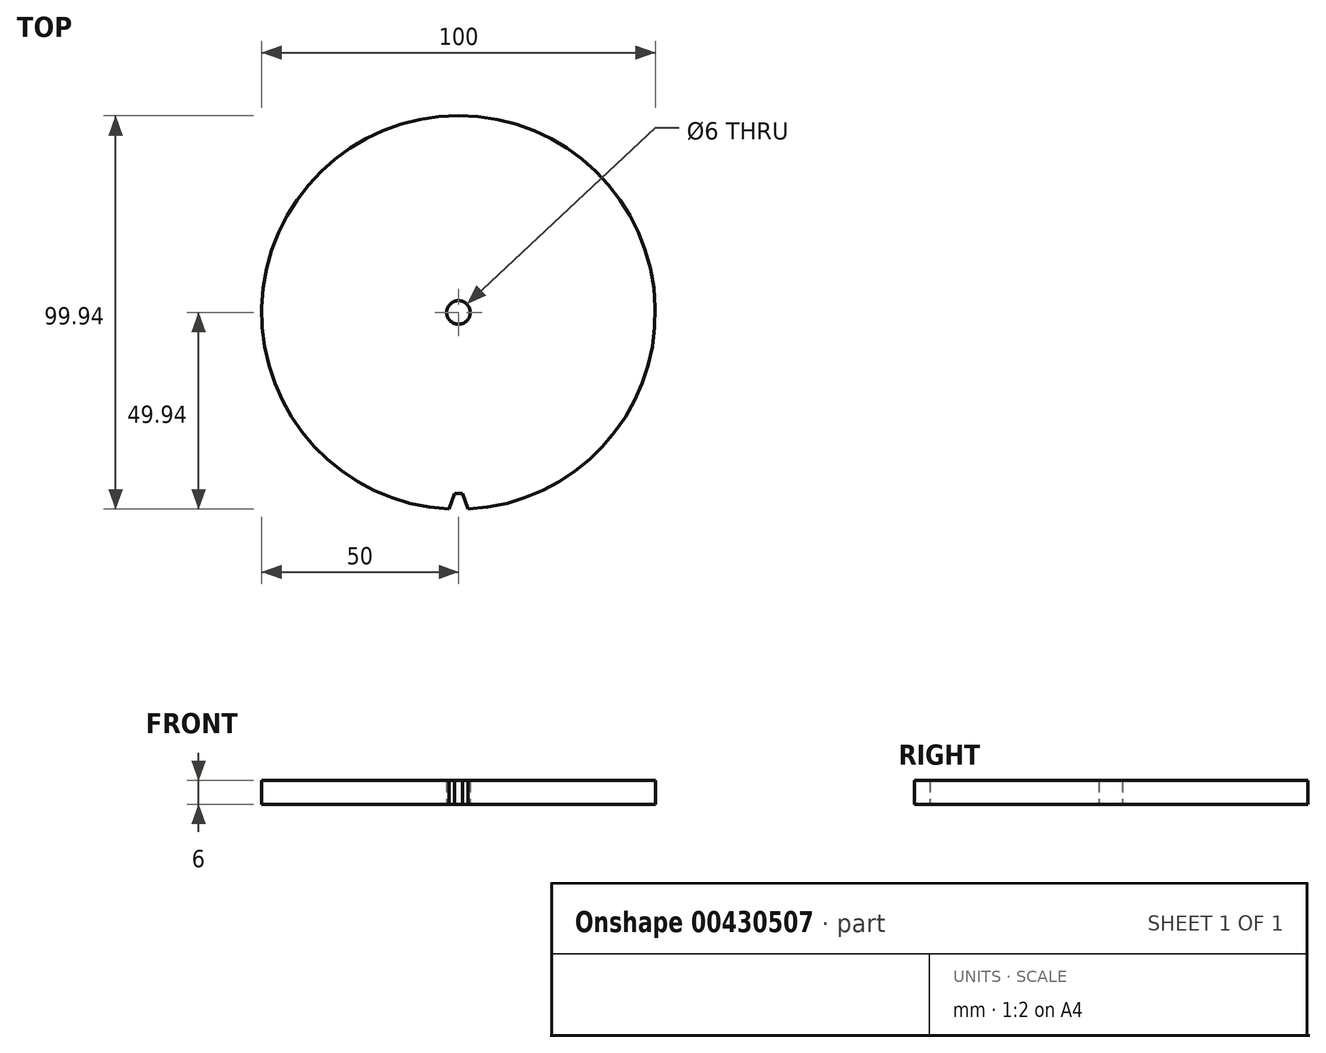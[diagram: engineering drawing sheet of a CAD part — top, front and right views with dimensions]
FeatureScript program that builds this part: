
annotation { "Feature Type Name" : "Feature", "Feature Type Description" : "" }
export const myFeature = defineFeature(function(context is Context, id is Id, definition is map)
    precondition{}
    {
        {
            var Q0;
            Q0=qCreatedBy(makeId("Top.planeOp"),FACE);
            var sketch = newSketch(context, id + "F0", { "sketchPlane" : qUnion([Q0])});
            skCircle(sketch, "E0", {"center": v(0, 0) * mm, "radius": 50 * mm});
            skSolve(sketch);
        }
        {
            var Q0;
            Q0 = qSketchRegion(id + "F0", true);
            extrude(context, id + "F1", {"entities" : qUnion([Q0]), "depth" : 6 * mm});
        }
        {
            var Q0;
            Q0=makeQuery(id+"F1.opExtrude","CAP_FACE",FACE,{"disambiguationData":[OSD([sQuery(id+"F0.wireOp",EDGE,"E0")])],"isStart":true});
            var sketch = newSketch(context, id + "F2", { "sketchPlane" : qUnion([Q0])});
            skCircle(sketch, "E1", {"center": v(0, 0) * mm, "radius": 3 * mm});
            skSolve(sketch);
        }
        {
            var Q0;
            Q0 = qSketchRegion(id + "F2", true);
            extrude(context, id + "F3", {"entities" : qUnion([Q0]), "operationType" : NewBodyOperationType.REMOVE, "endBound" : BoundingType.UP_TO_NEXT, "oppositeDirection" : true, "depth" : 25 * mm});
        }
        {
            var Q0;
            Q0=makeQuery(id+"F1.opExtrude","CAP_FACE",FACE,{"disambiguationData":[OSD([sQuery(id+"F0.wireOp",EDGE,"E0")])],"isStart":true});
            var sketch = newSketch(context, id + "F4", { "sketchPlane" : qUnion([Q0])});
            skCircle(sketch, "E2", {"center": v(0, 0) * mm, "radius": 46 * mm, "construction": true});
            skLineSegment(sketch, "E3", {"start": v(1, 45.99) * mm, "end": v(2.44, 49.94) * mm});
            skLineSegment(sketch, "E4", {"start": v(-1, 45.99) * mm, "end": v(-2.44, 49.94) * mm});
            skLineSegment(sketch, "E5", {"start": v(-1, 45.99) * mm, "end": v(1, 45.99) * mm});
            skArc(sketch, "E6", {"start": v(2.44, 49.94) * mm, "mid": v(0, 50.73) * mm, "end": v(-2.44, 49.94) * mm});
            skSolve(sketch);
        }
        {
            var Q0;
            {var subQ0=sQuery(id+"F4.wireOp",EDGE,"E3");Q0=makeQuery(id+"F4.imprint","IMPRINT",FACE,{"disambiguationData":[TD([[makeQuery(id+"F4.imprint","IMPRINT",EDGE,{"derivedFrom":subQ0}),1.0]])]});}
            extrude(context, id + "F5", {"entities" : qUnion([Q0]), "operationType" : NewBodyOperationType.REMOVE, "endBound" : BoundingType.UP_TO_NEXT, "oppositeDirection" : true, "depth" : 25 * mm});
        }
    });
